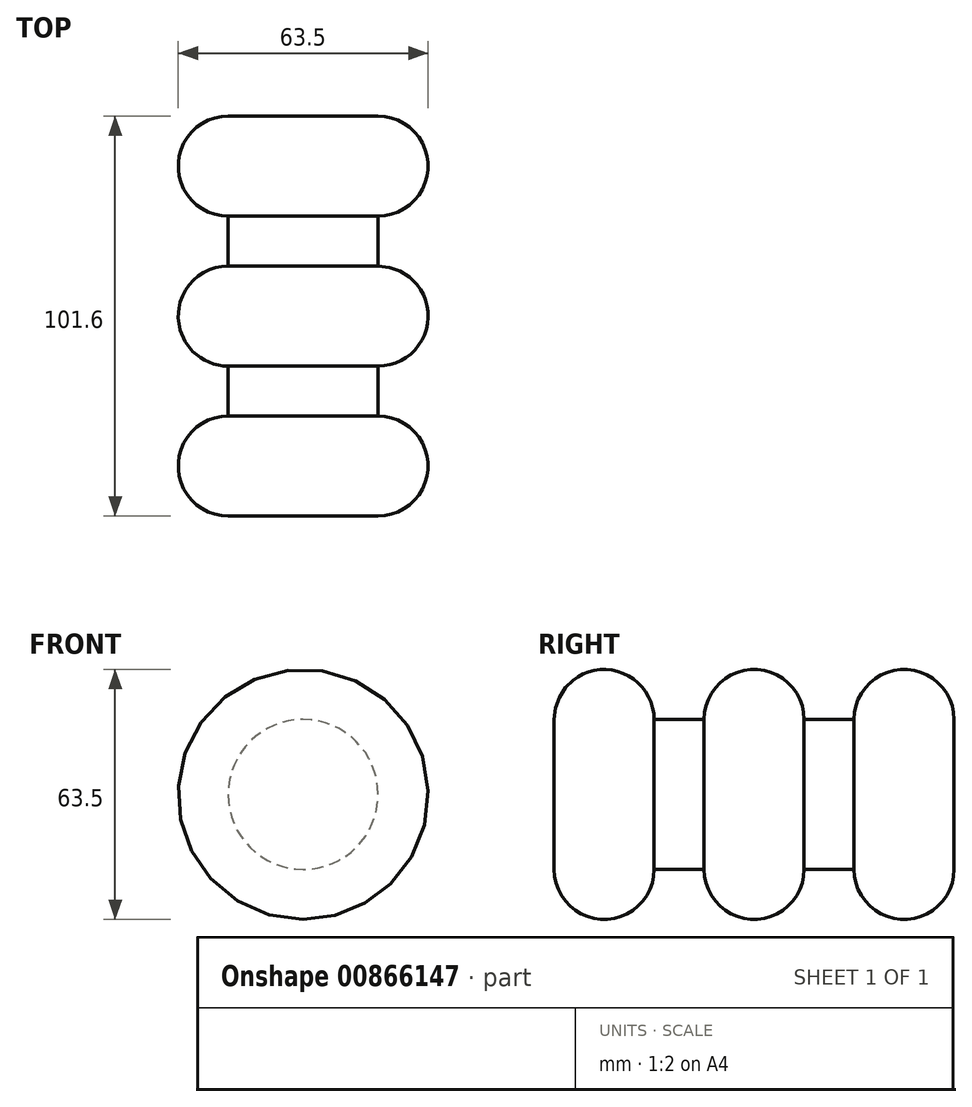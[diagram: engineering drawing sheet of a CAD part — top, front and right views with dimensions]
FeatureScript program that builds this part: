
annotation { "Feature Type Name" : "Feature", "Feature Type Description" : "" }
export const myFeature = defineFeature(function(context is Context, id is Id, definition is map)
    precondition{}
    {
        {
            var Q0;
            Q0=qCreatedBy(makeId("Top.planeOp"),FACE);
            var sketch = newSketch(context, id + "F0", { "sketchPlane" : qUnion([Q0])});
            skLineSegment(sketch, "E0.bottom", {"start": v(0, 0) * mm, "end": v(19.05, 0) * mm});
            skLineSegment(sketch, "E0.top", {"start": v(0, 101.6) * mm, "end": v(19.05, 101.6) * mm});
            skLineSegment(sketch, "E0.left", {"start": v(0, 0) * mm, "end": v(0, 101.6) * mm});
            skLineSegment(sketch, "E0.right", {"start": v(19.05, 0) * mm, "end": v(19.05, 101.6) * mm});
            skCircle(sketch, "E1", {"center": v(19.05, 88.9) * mm, "radius": 12.7 * mm});
            skCircle(sketch, "E2", {"center": v(19.05, 50.8) * mm, "radius": 12.7 * mm});
            skCircle(sketch, "E3", {"center": v(19.05, 12.7) * mm, "radius": 12.7 * mm});
            skSolve(sketch);
        }
        {
            var Q0;
            Q0 = qSketchRegion(id + "F0", true);
            var Q1;
            Q1=sQuery(id+"F0.wireOp",EDGE,"E0.left");
            revolve(context, id + "F1", {"surfaceOperationType" : NewSurfaceOperationType.NEW, "entities" : qUnion([Q0]), "axis" : qUnion([Q1]), "revolveType" : RevolveType.FULL});
        }
    });
